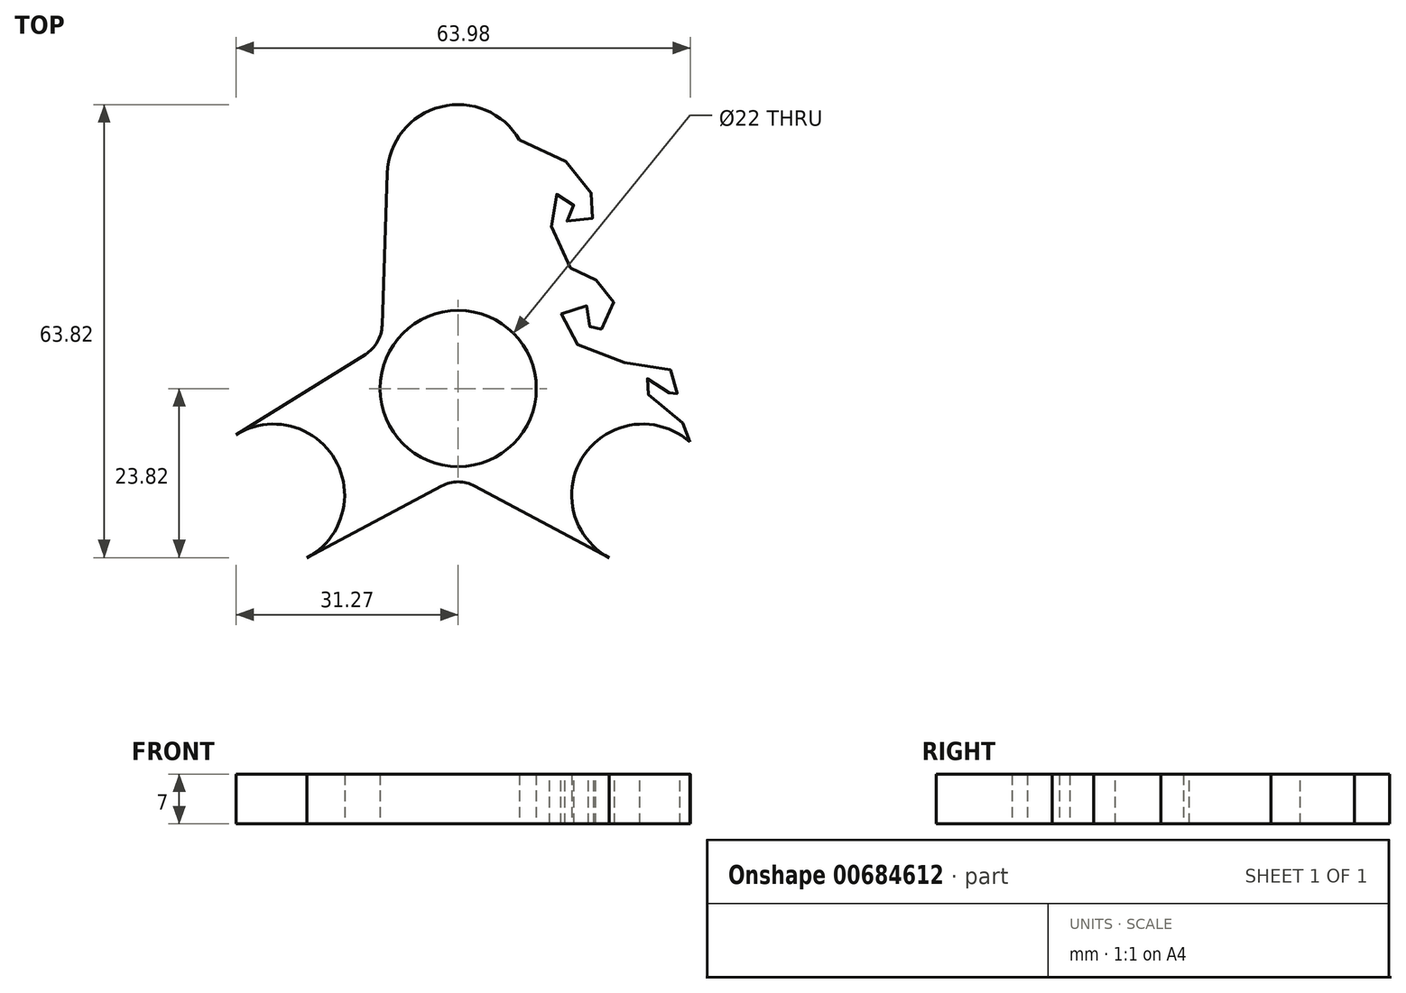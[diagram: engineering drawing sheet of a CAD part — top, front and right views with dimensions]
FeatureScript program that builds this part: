
annotation { "Feature Type Name" : "Feature", "Feature Type Description" : "" }
export const myFeature = defineFeature(function(context is Context, id is Id, definition is map)
    precondition{}
    {
        {
            var Q0;
            Q0=qCreatedBy(makeId("Top.planeOp"),FACE);
            var sketch = newSketch(context, id + "F0", { "sketchPlane" : qUnion([Q0])});
            skCircle(sketch, "E0", {"center": v(0, 0) * mm, "radius": 11 * mm});
            skLineSegment(sketch, "E1", {"start": v(-51.96, 30) * mm, "end": v(51.96, -30) * mm, "construction": true});
            skLineSegment(sketch, "E2.MirrorCS", {"start": v(51.96, 30) * mm, "end": v(-51.96, -30) * mm, "construction": true});
            skCircle(sketch, "E3", {"center": v(0, 30) * mm, "radius": 10 * mm});
            skCircle(sketch, "E4.MirrorC", {"center": v(-25.98, -15) * mm, "radius": 10 * mm});
            skCircle(sketch, "E5.MirrorC", {"center": v(25.98, -15) * mm, "radius": 10 * mm});
            skLineSegment(sketch, "E6", {"start": v(-10, 30.33) * mm, "end": v(-10.7, 8.9) * mm});
            skLineSegment(sketch, "E7", {"start": v(-13.06, 4.82) * mm, "end": v(-31.27, -6.51) * mm});
            skLineSegment(sketch, "E8", {"start": v(10, 30.33) * mm, "end": v(10.7, 8.9) * mm});
            skLineSegment(sketch, "E9.MirrorCS", {"start": v(-21.27, -23.82) * mm, "end": v(-2.35, -13.73) * mm});
            skLineSegment(sketch, "E10.MirrorCS", {"start": v(21.27, -23.82) * mm, "end": v(2.35, -13.73) * mm});
            skLineSegment(sketch, "E11.MirrorCS", {"start": v(31.27, -6.51) * mm, "end": v(13.06, 4.82) * mm});
            skPoint(sketch, "E12.newPointA", {"position": v(-11, 0) * mm});
            skArc(sketch, "E12.filletArc", {"start": v(-13.06, 4.82) * mm, "mid": v(-11.38, 6.57) * mm, "end": v(-10.7, 8.9) * mm});
            skPoint(sketch, "E13.newPointA", {"position": v(5.5, 9.53) * mm});
            skPoint(sketch, "E13.newPointB", {"position": v(11, 0) * mm});
            skArc(sketch, "E13.filletArc", {"start": v(10.7, 8.9) * mm, "mid": v(11.38, 6.57) * mm, "end": v(13.06, 4.82) * mm});
            skPoint(sketch, "E14.newPointA", {"position": v(5.5, -9.53) * mm});
            skPoint(sketch, "E14.newPointB", {"position": v(-5.5, -9.53) * mm});
            skArc(sketch, "E14.filletArc", {"start": v(2.35, -13.73) * mm, "mid": v(0, -13.14) * mm, "end": v(-2.35, -13.73) * mm});
            skFitSpline(sketch, "E15", {"points": [v(8.64, 35.04) * mm, v(18.82, 27.4) * mm, v(18.54, 23.7) * mm, v(15.04, 23.89) * mm, v(16.33, 26.2) * mm, v(13.52, 27.2) * mm, v(15.59, 17.25) * mm, v(20.2, 14.85) * mm, v(21.64, 9.89) * mm, v(18.36, 7.94) * mm, v(19, 10.97) * mm, v(14.85, 11.07) * mm, v(19, 4.8) * mm, v(31.05, 1.68) * mm, v(30.1, -1.69) * mm, v(29.07, 0.55) * mm, v(25.6, 0.94) * mm, v(32.02, -5.29) * mm, v(32.62, -7.53) * mm], "startDerivative": vector(180.95, -37.43) * mm, "endDerivative": vector(-10.53, -79.98) * mm});
            skSolve(sketch);
        }
        {
            var Q0;
            Q0=makeQuery(id+"F0.imprint","IMPRINT",FACE,{"disambiguationData":[TD([[makeQuery(id+"F0.imprint","IMPRINT",EDGE,{"derivedFrom":sQuery(id+"F0.wireOp",EDGE,"E0")}),-1.0]])]});
            var Q1;
            {var subQ0=sQuery(id+"F0.wireOp",EDGE,"E3");var subQ1=makeQuery(id+"F0.imprint","INTERSECT",VERTEX,{"derivedFrom":[subQ0,sQuery(id+"F0.wireOp",EDGE,"E8")]});Q1=makeQuery(id+"F0.imprint","IMPRINT",FACE,{"disambiguationData":[TD([[makeQuery(id+"F0.imprint","IMPRINT",EDGE,{"disambiguationData":[TD([[subQ1,-1.0]])],"derivedFrom":subQ0}),1.0]])]});}
            var Q2;
            {var subQ0=sQuery(id+"F0.wireOp",EDGE,"E4.MirrorC");var subQ1=makeQuery(id+"F0.imprint","INTERSECT",VERTEX,{"derivedFrom":[subQ0,sQuery(id+"F0.wireOp",EDGE,"E7")]});Q2=makeQuery(id+"F0.imprint","IMPRINT",FACE,{"disambiguationData":[TD([[makeQuery(id+"F0.imprint","IMPRINT",EDGE,{"disambiguationData":[TD([[subQ1,1.0]])],"derivedFrom":subQ0}),-1.0]])]});}
            var Q3;
            {var subQ0=sQuery(id+"F0.wireOp",EDGE,"E5.MirrorC");var subQ1=makeQuery(id+"F0.imprint","INTERSECT",VERTEX,{"derivedFrom":[subQ0,sQuery(id+"F0.wireOp",EDGE,"E11.MirrorCS")]});Q3=makeQuery(id+"F0.imprint","IMPRINT",FACE,{"disambiguationData":[TD([[makeQuery(id+"F0.imprint","IMPRINT",EDGE,{"disambiguationData":[TD([[subQ1,-1.0]])],"derivedFrom":subQ0}),-1.0]])]});}
            var Q4;
            {var subQ5=sQuery(id+"F0.wireOp",EDGE,"lwHCKfIK-zS6e-CTAC-9HsI-oUIeT1y9pyuL");Q4=makeQuery(id+"F0.imprint","IMPRINT",FACE,{"disambiguationData":[TD([[makeQuery(id+"F0.imprint","IMPRINT",EDGE,{"derivedFrom":subQ5}),1.0]])]});}
            var Q5;
            {var subQ1=sQuery(id+"F0.wireOp",EDGE,"E8");Q5=makeQuery(id+"F0.imprint","IMPRINT",FACE,{"disambiguationData":[TD([[makeQuery(id+"F0.imprint","IMPRINT",EDGE,{"derivedFrom":subQ1}),1.0]])]});}
            extrude(context, id + "F1", {"entities" : qUnion([Q0, Q1, Q2, Q3, Q4, Q5]), "depth" : 7 * mm, "offsetDistance" : 25 * mm});
        }
    });
